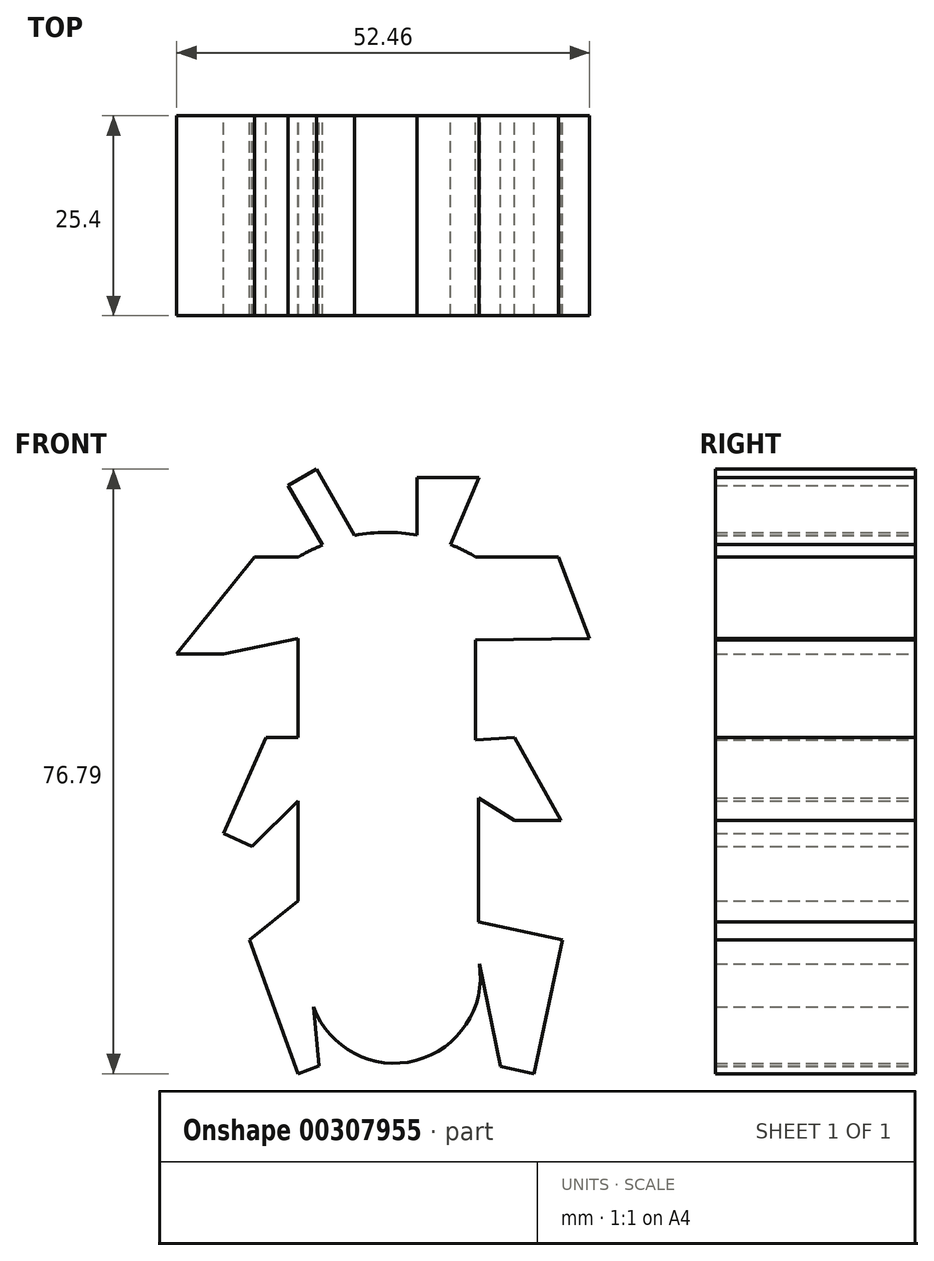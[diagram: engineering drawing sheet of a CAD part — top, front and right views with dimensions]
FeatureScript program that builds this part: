
annotation { "Feature Type Name" : "Feature", "Feature Type Description" : "" }
export const myFeature = defineFeature(function(context is Context, id is Id, definition is map)
    precondition{}
    {
        {
            var Q0;
            Q0=qCreatedBy(makeId("Front.planeOp"),FACE);
            var sketch = newSketch(context, id + "F0", { "sketchPlane" : qUnion([Q0])});
            skArc(sketch, "E0", {"start": v(-13.74, 0) * mm, "mid": v(-2.93, -12.64) * mm, "end": v(7.89, 0) * mm});
            skLineSegment(sketch, "E1", {"start": v(-15.15, 7.96) * mm, "end": v(-15.15, 20.66) * mm});
            skLineSegment(sketch, "E2", {"start": v(7.8, 5.3) * mm, "end": v(7.8, 21.07) * mm});
            skLineSegment(sketch, "E3", {"start": v(-15.15, 7.96) * mm, "end": v(-21.32, 3.03) * mm});
            skLineSegment(sketch, "E4", {"start": v(-21.32, 3.03) * mm, "end": v(-15.15, -13.96) * mm});
            skLineSegment(sketch, "E5", {"start": v(-15.15, -13.96) * mm, "end": v(-12.44, -12.97) * mm});
            skLineSegment(sketch, "E6", {"start": v(-12.44, -12.97) * mm, "end": v(-13.74, 0) * mm});
            skLineSegment(sketch, "E7", {"start": v(7.8, 5.3) * mm, "end": v(18.43, 3.03) * mm});
            skLineSegment(sketch, "E8", {"start": v(18.43, 3.03) * mm, "end": v(14.81, -13.96) * mm});
            skLineSegment(sketch, "E9", {"start": v(14.81, -13.96) * mm, "end": v(10.6, -13.06) * mm});
            skLineSegment(sketch, "E10", {"start": v(10.6, -13.06) * mm, "end": v(7.89, 0) * mm});
            skLineSegment(sketch, "E11", {"start": v(-15.15, 28.77) * mm, "end": v(-15.15, 41.3) * mm});
            skLineSegment(sketch, "E12", {"start": v(7.38, 28.44) * mm, "end": v(7.38, 41.14) * mm});
            skLineSegment(sketch, "E13", {"start": v(-15.15, 28.77) * mm, "end": v(-19.18, 28.77) * mm});
            skLineSegment(sketch, "E14", {"start": v(-19.18, 28.77) * mm, "end": v(-24.62, 16.56) * mm});
            skLineSegment(sketch, "E15", {"start": v(-24.62, 16.56) * mm, "end": v(-20.95, 14.92) * mm});
            skLineSegment(sketch, "E16", {"start": v(-20.95, 14.92) * mm, "end": v(-15.15, 20.66) * mm});
            skLineSegment(sketch, "E17", {"start": v(7.38, 28.44) * mm, "end": v(12.33, 28.77) * mm});
            skLineSegment(sketch, "E18", {"start": v(12.33, 28.77) * mm, "end": v(18.27, 18.21) * mm});
            skLineSegment(sketch, "E19", {"start": v(18.27, 18.21) * mm, "end": v(12.33, 18.21) * mm});
            skLineSegment(sketch, "E20", {"start": v(12.33, 18.21) * mm, "end": v(7.8, 21.07) * mm});
            skArc(sketch, "E21", {"start": v(7.38, 51.7) * mm, "mid": v(-3.84, 54.8) * mm, "end": v(-15.05, 51.7) * mm});
            skLineSegment(sketch, "E22", {"start": v(-15.05, 51.7) * mm, "end": v(-20.66, 51.7) * mm});
            skLineSegment(sketch, "E23", {"start": v(-20.66, 51.7) * mm, "end": v(-30.56, 39.33) * mm});
            skLineSegment(sketch, "E24", {"start": v(-30.56, 39.33) * mm, "end": v(-24.62, 39.33) * mm});
            skLineSegment(sketch, "E25", {"start": v(-24.62, 39.33) * mm, "end": v(-15.15, 41.3) * mm});
            skLineSegment(sketch, "E26", {"start": v(7.38, 51.7) * mm, "end": v(17.94, 51.7) * mm});
            skLineSegment(sketch, "E27", {"start": v(17.94, 51.7) * mm, "end": v(21.9, 41.3) * mm});
            skLineSegment(sketch, "E28", {"start": v(21.9, 41.3) * mm, "end": v(7.38, 41.14) * mm});
            skLineSegment(sketch, "E29", {"start": v(-7.94, 54.42) * mm, "end": v(-12.82, 62.83) * mm});
            skLineSegment(sketch, "E30", {"start": v(-12.82, 62.83) * mm, "end": v(-16.41, 60.74) * mm});
            skLineSegment(sketch, "E31", {"start": v(-16.41, 60.74) * mm, "end": v(-12.04, 53.2) * mm});
            skLineSegment(sketch, "E32", {"start": v(4.2, 53.27) * mm, "end": v(7.88, 61.78) * mm});
            skPoint(sketch, "E32.endSnap0", {"position": v(-14.62, 61.78) * mm});
            skLineSegment(sketch, "E33", {"start": v(7.88, 61.78) * mm, "end": v(0, 61.78) * mm});
            skLineSegment(sketch, "E34", {"start": v(0, 61.78) * mm, "end": v(0, 54.42) * mm});
            skSolve(sketch);
        }
        {
            var Q0;
            Q0 = qSketchRegion(id + "F0", true);
            extrude(context, id + "F1", {"entities" : qUnion([Q0]), "depth" : 25.4 * mm});
        }
    });
